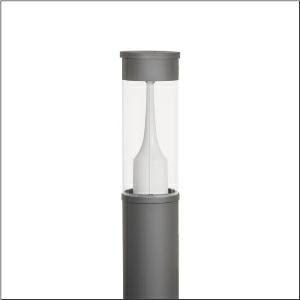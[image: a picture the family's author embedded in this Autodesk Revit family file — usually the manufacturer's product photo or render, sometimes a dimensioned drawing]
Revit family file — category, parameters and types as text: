
# Revit family: city-light_260_iq___st1_2a_5xa5295ef14h_2f06
name_source: partatom
category: Lighting Fixtures
units: mm (PartAtom-declared; Revit-internal decimal feet)

## family parameters
Cut with Voids When Loaded = No
Host = Face
Light Source = No
Part Type = Normal
Room Calculation Point = No
Round Connector Dimension = Use Diameter
Shared = No

## types (1)
- --- (1 x LED, 1540 lm, 10.5 W, 3000K)
    Apparent Load = 11 VA
    CIE Flux Codes = 22 61 93 96 100
    Color Rendering = 70
    Color Temperature = 3000K
    Default Elevation = 1800 mm
    Description = City-Light 260 iQ, light pillar, Module 540 iQ-SR, primary light control with 3 zone facetted reflector, of plastic, silver coated, highly specular, structured, primary optical cover: cover, of PMMA, transparent, light distribution: ST1.2a, primary light characteristic: asymmetric, LED, High Power LED, rated luminous flux: 1.540lm, luminous efficacy: 147lm/W, light colour: 730, colour temperature: 3000K, control gear: iQ Street-Remote, control: Auto-Match, Temp-Guard, Lumen-Switch, Night-Set, Smart-Wire, Light-Fading, Desk-Remote (wireless, voltage-free reading and setting of iQ features in the workshop via application-optimized NFC function/RFID function), optimised constant luminous flux control (CLO 2.0), Street-Remote, pre-setting: logarithmic dimming characteristic, with terminal, 6-pole, max. 2.5mm², mains connection: 230..240V, AC, 50/60Hz, start of lifetime: 11W, end of service life: 11W, reduction: 5W, luminaire housing, cylindrical, of extruded aluminium section, coated, Siteco® metallic grey (DB 702S), length: 2.600mm, diameter: 200mm, Module 540 iQ-SR, traffic white (RAL 9016), equipment: standard, protection rating (complete): IP65, insulation class (complete): insulation class II (safety insulation), certification: CE, ENEC, VDE, packaging unit: 1 piece

Light Distribution: ST1.2a
    Height = 500 mm
    Lamp = 1 x LED
    Lamp Light Flux = 1540 lm
    Lamp Power = 10.5 W
    Lamp count = 1
    Length = 200 mm  [stored 0.656168 ft]
    Luminous efficacy = 147 lm/W
    Manufacturer = Siteco
    ModVariant = No
    Model = 5XA5295EF14H
    Mounting Place = Floor
    Mounting Type = Freestanding
    Number of Poles = 1
    OnlyDefault = Yes
    Power Factor = 1
    Product Name = City-Light 260 iQ | ST1.2a
    Product group = light pillar
    ProductGroupID = 1301
    Protection Class = Protection class II
    Protection Degree = IP 65
    RLX_Detail_Level = 1
    RLX_Emergency_Light_Flux = 0 lm
    RLX_Emergency_Type = 0
    RLX_Emergency_Type_DB = No
    RlxData = <blob elided: 60605 chars, md5=9e537ebe>
    Socket = socket
    Standby Power = 0 W
    System Light Flux = 1540 lm
    System Power = 11 W
    Type Comments = factory setting: luminous flux: 100 % | dim-lin: 254 | 419 mA
    Type Image = l_1006918.jpg
    URL = http://relux.com
    VarID = @adj_162463
    Voltage = 0 V
    Weight = 0.00 kg
    Width = 0 mm  [stored 0 ft]

note: [stored X ft] marks values corroborated as IEEE doubles in the binary element streams (Revit-internal decimal feet)

## geometry (parser evidence)
native form markers: Blend x4, Sweep x9
no freeform markers — native parametric forms only
